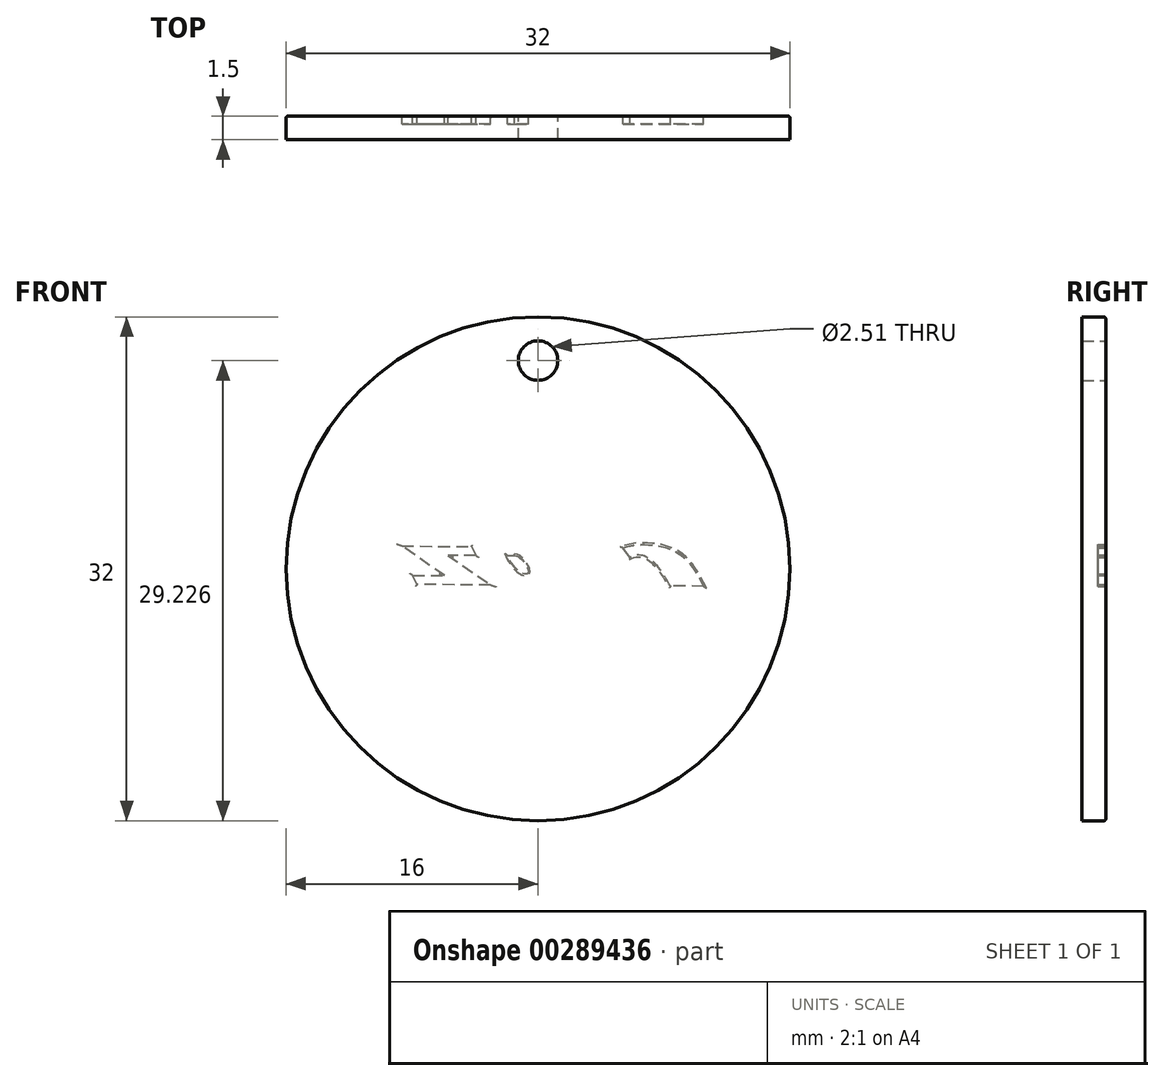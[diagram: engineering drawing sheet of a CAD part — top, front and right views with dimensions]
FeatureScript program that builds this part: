
annotation { "Feature Type Name" : "Feature", "Feature Type Description" : "" }
export const myFeature = defineFeature(function(context is Context, id is Id, definition is map)
    precondition{}
    {
        {
            var Q0;
            Q0=qCreatedBy(makeId("Front.planeOp"),FACE);
            var sketch = newSketch(context, id + "F0", { "sketchPlane" : qUnion([Q0])});
            skCircle(sketch, "E0", {"center": v(0, 0) * mm, "radius": 16 * mm});
            skSolve(sketch);
        }
        {
            var Q0;
            Q0=makeQuery(id+"F0.imprint","IMPRINT",FACE,{"disambiguationData":[TD([[makeQuery(id+"F0.imprint","IMPRINT",EDGE,{"derivedFrom":sQuery(id+"F0.wireOp",EDGE,"E0")}),1.0]])]});
            extrude(context, id + "F1", {"entities" : qUnion([Q0]), "depth" : 1.5 * mm});
        }
        {
            var Q0;
            Q0=qCreatedBy(makeId("Front.planeOp"),FACE);
            var sketch = newSketch(context, id + "F2", { "sketchPlane" : qUnion([Q0])});
            skArc(sketch, "E1.MirrorCS", {"start": v(1.25, -1.6) * mm, "mid": v(1.25, -1.68) * mm, "end": v(1.2, -1.73) * mm});
            skFitSpline(sketch, "E2.MirrorCS", {"points": [v(1.2, -1.73) * mm, v(1.16, -1.75) * mm, v(1.1, -1.78) * mm, v(1.05, -1.8) * mm, v(1.01, -1.82) * mm, v(0.98, -1.83) * mm, v(0.91, -1.86) * mm, v(0.85, -1.88) * mm, v(0.81, -1.9) * mm]});
            skFitSpline(sketch, "E3.MirrorCS", {"points": [v(0.8, -1.22) * mm, v(0.89, -1.2) * mm, v(0.97, -1.17) * mm, v(1.05, -1.15) * mm]});
            skFitSpline(sketch, "E4.MirrorCS", {"points": [v(1.05, -1.15) * mm, v(1.12, -1.3) * mm, v(1.18, -1.45) * mm, v(1.25, -1.6) * mm]});
            skFitSpline(sketch, "E5.MirrorCS", {"points": [v(-1.95, 0.85) * mm, v(-1.8, 0.85) * mm, v(-1.65, 0.85) * mm, v(-1.5, 0.85) * mm]});
            skFitSpline(sketch, "E6.MirrorCS", {"points": [v(-1.5, 0.85) * mm, v(-1.45, 0.84) * mm, v(-1.4, 0.82) * mm, v(-1.34, 0.8) * mm, v(-1.3, 0.8) * mm, v(-1.3, 0.79) * mm, v(-1.27, 0.78) * mm, v(-1.24, 0.76) * mm, v(-1.2, 0.74) * mm, v(-1.16, 0.7) * mm, v(-1.1, 0.67) * mm, v(-1.08, 0.64) * mm, v(-1.03, 0.6) * mm, v(-0.97, 0.53) * mm, v(-0.9, 0.45) * mm, v(-0.85, 0.37) * mm, v(-0.8, 0.3) * mm, v(-0.75, 0.22) * mm, v(-0.72, 0.16) * mm, v(-0.69, 0.1) * mm, v(-0.67, 0.05) * mm, v(-0.65, 0.02) * mm, v(-0.64, 0) * mm, v(-0.64, -0.02) * mm, v(-0.64, -0.03) * mm, v(-0.63, -0.05) * mm, v(-0.63, -0.07) * mm, v(-0.62, -0.1) * mm, v(-0.6, -0.15) * mm, v(-0.61, -0.2) * mm, v(-0.62, -0.22) * mm, v(-0.62, -0.24) * mm, v(-0.63, -0.27) * mm, v(-0.65, -0.3) * mm, v(-0.68, -0.32) * mm, v(-0.72, -0.33) * mm, v(-0.76, -0.34) * mm, v(-0.78, -0.34) * mm, v(-0.8, -0.34) * mm, v(-0.8, -0.34) * mm, v(-0.82, -0.33) * mm, v(-0.85, -0.33) * mm, v(-0.89, -0.32) * mm, v(-0.93, -0.3) * mm, v(-0.97, -0.29) * mm, v(-1, -0.27) * mm, v(-1.02, -0.26) * mm, v(-1.06, -0.24) * mm, v(-1.1, -0.21) * mm, v(-1.19, -0.16) * mm, v(-1.27, -0.1) * mm, v(-1.35, -0.04) * mm, v(-1.41, 0.03) * mm, v(-1.46, 0.08) * mm, v(-1.5, 0.12) * mm, v(-1.53, 0.16) * mm, v(-1.58, 0.22) * mm, v(-1.63, 0.29) * mm, v(-1.68, 0.36) * mm, v(-1.72, 0.41) * mm, v(-1.74, 0.44) * mm, v(-1.75, 0.47) * mm, v(-1.76, 0.49) * mm, v(-1.78, 0.52) * mm, v(-1.8, 0.56) * mm, v(-1.86, 0.67) * mm, v(-1.91, 0.77) * mm, v(-1.95, 0.85) * mm]});
            skFitSpline(sketch, "E7.MirrorCS", {"points": [v(-3.92, 1.36) * mm, v(-3.03, 1.37) * mm, v(-2.15, 1.39) * mm, v(-1.26, 1.4) * mm]});
            skFitSpline(sketch, "E8.MirrorCS", {"points": [v(-5.73, 0.85) * mm, v(-4.83, 0.23) * mm, v(-3.92, -0.4) * mm, v(-3.02, -1.03) * mm]});
            skFitSpline(sketch, "E9.MirrorCS", {"points": [v(-4.22, 1.42) * mm, v(-4.13, 1.23) * mm, v(-4.04, 1.04) * mm, v(-3.95, 0.84) * mm]});
            skFitSpline(sketch, "E10.MirrorCS", {"points": [v(0.82, -0.97) * mm, v(0.78, -1) * mm, v(0.69, -1.03) * mm, v(0.59, -1.05) * mm, v(0.52, -1.06) * mm, v(0.49, -1.06) * mm, v(0.42, -1.07) * mm, v(0.32, -1.07) * mm, v(0.21, -1.07) * mm, v(0.12, -1.07) * mm, v(0, -1.06) * mm, v(-0.14, -1.04) * mm, v(-0.28, -1.01) * mm, v(-0.4, -0.98) * mm, v(-0.54, -0.94) * mm, v(-0.64, -0.9) * mm, v(-0.73, -0.85) * mm, v(-0.78, -0.82) * mm, v(-0.82, -0.8) * mm, v(-0.84, -0.79) * mm, v(-0.85, -0.78) * mm, v(-0.86, -0.78) * mm, v(-0.87, -0.77) * mm, v(-0.9, -0.76) * mm, v(-0.93, -0.73) * mm, v(-1, -0.69) * mm, v(-1.1, -0.62) * mm, v(-1.2, -0.55) * mm, v(-1.25, -0.52) * mm]});
            skFitSpline(sketch, "E11.MirrorCS", {"points": [v(-2.82, -0.75) * mm, v(-3.2, -0.03) * mm, v(-3.57, 0.68) * mm, v(-3.92, 1.36) * mm]});
            skFitSpline(sketch, "E12.MirrorCS", {"points": [v(-1.26, 1.4) * mm, v(-1.06, 1.4) * mm, v(-0.77, 1.36) * mm, v(-0.44, 1.3) * mm, v(-0.28, 1.25) * mm, v(-0.2, 1.22) * mm, v(-0.13, 1.2) * mm, v(-0.05, 1.17) * mm, v(0.04, 1.13) * mm, v(0.15, 1.08) * mm, v(0.26, 1.03) * mm, v(0.34, 0.98) * mm, v(0.4, 0.95) * mm, v(0.46, 0.9) * mm, v(0.52, 0.87) * mm, v(0.57, 0.83) * mm, v(0.6, 0.8) * mm, v(0.64, 0.78) * mm, v(0.65, 0.77) * mm, v(0.68, 0.74) * mm, v(0.74, 0.69) * mm, v(0.8, 0.63) * mm, v(0.84, 0.58) * mm]});
            skFitSpline(sketch, "E13.MirrorCS", {"points": [v(-7.96, -0.42) * mm, v(-7.29, -0.42) * mm, v(-6.61, -0.42) * mm, v(-5.94, -0.43) * mm]});
            skFitSpline(sketch, "E14.MirrorCS", {"points": [v(8.4, -1.1) * mm, v(8.33, -0.97) * mm, v(8.22, -0.78) * mm, v(8.06, -0.53) * mm, v(7.95, -0.35) * mm, v(7.83, -0.15) * mm, v(7.7, 0.02) * mm, v(7.58, 0.16) * mm, v(7.5, 0.26) * mm, v(7.45, 0.3) * mm, v(7.41, 0.34) * mm, v(7.36, 0.4) * mm, v(7.3, 0.45) * mm, v(7.2, 0.54) * mm, v(7.04, 0.65) * mm, v(6.9, 0.74) * mm, v(6.79, 0.79) * mm, v(6.72, 0.81) * mm, v(6.68, 0.83) * mm, v(6.62, 0.84) * mm, v(6.55, 0.86) * mm, v(6.46, 0.87) * mm, v(6.37, 0.88) * mm, v(6.3, 0.88) * mm, v(6.24, 0.87) * mm, v(6.2, 0.86) * mm, v(6.14, 0.85) * mm, v(6.02, 0.82) * mm, v(5.9, 0.77) * mm, v(5.83, 0.73) * mm]});
            skFitSpline(sketch, "E15.MirrorCS", {"points": [v(10.52, -1.1) * mm, v(9.81, -1.1) * mm, v(9.1, -1.1) * mm, v(8.4, -1.1) * mm]});
            skFitSpline(sketch, "E16.MirrorCS", {"points": [v(0.82, 0.62) * mm, v(0.93, 0.48) * mm, v(1.07, 0.28) * mm, v(1.17, 0.04) * mm, v(1.2, -0.08) * mm, v(1.21, -0.15) * mm, v(1.22, -0.2) * mm, v(1.22, -0.27) * mm, v(1.23, -0.35) * mm, v(1.22, -0.44) * mm, v(1.2, -0.55) * mm, v(1.15, -0.68) * mm, v(1.04, -0.83) * mm, v(0.9, -0.93) * mm, v(0.82, -0.97) * mm]});
            skFitSpline(sketch, "E17.MirrorCS", {"points": [v(-8.64, 1.44) * mm, v(-7.17, 1.44) * mm, v(-5.7, 1.43) * mm, v(-4.22, 1.42) * mm]});
            skFitSpline(sketch, "E18.MirrorCS", {"points": [v(-3.02, -1.03) * mm, v(-4.58, -1.02) * mm, v(-6.14, -1) * mm, v(-7.7, -1) * mm]});
            skFitSpline(sketch, "E19.MirrorCS", {"points": [v(5.83, 0.73) * mm, v(5.68, 0.93) * mm, v(5.53, 1.13) * mm, v(5.38, 1.33) * mm]});
            skFitSpline(sketch, "E20.MirrorCS", {"points": [v(-3.95, 0.84) * mm, v(-4.54, 0.85) * mm, v(-5.14, 0.85) * mm, v(-5.73, 0.85) * mm]});
            skFitSpline(sketch, "E21.MirrorCS", {"points": [v(-1.25, -0.52) * mm, v(-1.24, -0.55) * mm, v(-1.21, -0.6) * mm, v(-1.17, -0.67) * mm, v(-1.14, -0.72) * mm, v(-1.13, -0.75) * mm, v(-1.11, -0.77) * mm, v(-1.1, -0.78) * mm, v(-1.1, -0.8) * mm, v(-1.08, -0.82) * mm, v(-1.05, -0.86) * mm, v(-1.01, -0.91) * mm, v(-0.96, -0.97) * mm, v(-0.9, -1.03) * mm, v(-0.8, -1.1) * mm, v(-0.68, -1.18) * mm, v(-0.56, -1.23) * mm, v(-0.47, -1.26) * mm, v(-0.42, -1.28) * mm, v(-0.38, -1.29) * mm, v(-0.34, -1.3) * mm, v(-0.3, -1.3) * mm, v(-0.21, -1.32) * mm, v(-0.12, -1.33) * mm, v(-0.01, -1.33) * mm, v(0.06, -1.33) * mm, v(0.13, -1.33) * mm, v(0.18, -1.32) * mm, v(0.2, -1.32) * mm, v(0.23, -1.32) * mm, v(0.24, -1.32) * mm, v(0.26, -1.32) * mm, v(0.3, -1.31) * mm, v(0.34, -1.3) * mm, v(0.41, -1.3) * mm, v(0.5, -1.28) * mm, v(0.64, -1.25) * mm, v(0.76, -1.23) * mm, v(0.82, -1.21) * mm]});
            skFitSpline(sketch, "E22.MirrorCS", {"points": [v(-7.7, -1) * mm, v(-7.79, -0.8) * mm, v(-7.87, -0.61) * mm, v(-7.96, -0.42) * mm]});
            skFitSpline(sketch, "E23.MirrorCS", {"points": [v(-5.94, -0.43) * mm, v(-6.84, 0.2) * mm, v(-7.74, 0.82) * mm, v(-8.64, 1.44) * mm]});
            skFitSpline(sketch, "E24.MirrorCS", {"points": [v(0.83, -1.89) * mm, v(0.7, -1.92) * mm, v(0.46, -1.95) * mm, v(0.1, -1.98) * mm, v(-0.14, -1.98) * mm, v(-0.35, -1.98) * mm, v(-0.54, -1.98) * mm, v(-0.72, -1.97) * mm, v(-0.88, -1.96) * mm, v(-1, -1.94) * mm, v(-1.1, -1.93) * mm, v(-1.16, -1.92) * mm, v(-1.2, -1.92) * mm, v(-1.21, -1.91) * mm, v(-1.25, -1.9) * mm, v(-1.3, -1.9) * mm, v(-1.37, -1.88) * mm, v(-1.47, -1.85) * mm, v(-1.6, -1.81) * mm, v(-1.76, -1.75) * mm, v(-1.9, -1.68) * mm, v(-2.05, -1.6) * mm, v(-2.16, -1.53) * mm, v(-2.27, -1.45) * mm, v(-2.36, -1.36) * mm, v(-2.46, -1.27) * mm, v(-2.53, -1.2) * mm, v(-2.58, -1.13) * mm, v(-2.62, -1.08) * mm, v(-2.66, -1.04) * mm, v(-2.68, -1) * mm, v(-2.7, -0.98) * mm, v(-2.7, -0.96) * mm, v(-2.73, -0.93) * mm, v(-2.76, -0.87) * mm, v(-2.8, -0.8) * mm, v(-2.82, -0.75) * mm]});
            skFitSpline(sketch, "E25.MirrorCS", {"points": [v(5.38, 1.33) * mm, v(5.48, 1.37) * mm, v(5.7, 1.44) * mm, v(6.02, 1.5) * mm, v(6.28, 1.52) * mm, v(6.5, 1.53) * mm, v(6.67, 1.54) * mm, v(6.82, 1.54) * mm, v(6.94, 1.53) * mm, v(7.04, 1.53) * mm, v(7.19, 1.52) * mm, v(7.43, 1.5) * mm, v(7.76, 1.45) * mm, v(8.07, 1.37) * mm, v(8.28, 1.3) * mm, v(8.38, 1.26) * mm, v(8.44, 1.23) * mm, v(8.48, 1.22) * mm, v(8.53, 1.2) * mm, v(8.6, 1.17) * mm, v(8.7, 1.12) * mm, v(8.85, 1.04) * mm, v(8.98, 0.95) * mm, v(9.08, 0.87) * mm, v(9.16, 0.81) * mm, v(9.22, 0.76) * mm, v(9.31, 0.68) * mm, v(9.43, 0.57) * mm, v(9.54, 0.44) * mm, v(9.62, 0.34) * mm, v(9.67, 0.29) * mm, v(9.7, 0.24) * mm, v(9.73, 0.2) * mm, v(9.77, 0.15) * mm, v(9.84, 0.06) * mm, v(9.92, -0.05) * mm, v(9.99, -0.16) * mm, v(10.04, -0.24) * mm, v(10.09, -0.3) * mm, v(10.12, -0.36) * mm, v(10.14, -0.39) * mm, v(10.15, -0.41) * mm, v(10.16, -0.42) * mm, v(10.17, -0.45) * mm, v(10.2, -0.48) * mm, v(10.23, -0.54) * mm, v(10.27, -0.62) * mm, v(10.33, -0.73) * mm, v(10.4, -0.89) * mm, v(10.48, -1.03) * mm, v(10.52, -1.1) * mm]});
            skFitSpline(sketch, "E26.MirrorC", {"points": [v(3.04, 1.45) * mm, v(3.14, 1.45) * mm, v(3.22, 1.44) * mm, v(3.34, 1.44) * mm, v(3.49, 1.43) * mm, v(3.64, 1.42) * mm, v(3.77, 1.4) * mm, v(3.86, 1.4) * mm, v(3.96, 1.38) * mm, v(4.1, 1.36) * mm, v(4.25, 1.33) * mm, v(4.39, 1.3) * mm, v(4.48, 1.27) * mm, v(4.54, 1.25) * mm, v(4.57, 1.24) * mm, v(4.62, 1.23) * mm, v(4.68, 1.2) * mm, v(4.78, 1.17) * mm, v(4.92, 1.1) * mm, v(5.08, 1.03) * mm, v(5.23, 0.94) * mm, v(5.38, 0.82) * mm, v(5.49, 0.73) * mm, v(5.57, 0.63) * mm, v(5.63, 0.56) * mm, v(5.7, 0.5) * mm, v(5.74, 0.42) * mm, v(5.79, 0.34) * mm, v(5.83, 0.26) * mm, v(5.87, 0.18) * mm, v(5.9, 0.06) * mm, v(5.93, -0.1) * mm, v(5.93, -0.24) * mm, v(5.9, -0.36) * mm, v(5.88, -0.44) * mm, v(5.84, -0.53) * mm, v(5.79, -0.6) * mm, v(5.74, -0.67) * mm, v(5.67, -0.74) * mm, v(5.61, -0.78) * mm, v(5.56, -0.82) * mm, v(5.52, -0.85) * mm, v(5.49, -0.87) * mm, v(5.44, -0.9) * mm, v(5.37, -0.93) * mm, v(5.3, -0.96) * mm, v(5.24, -0.98) * mm, v(5.19, -1) * mm, v(5.15, -1) * mm, v(5.1, -1.02) * mm, v(5.03, -1.04) * mm, v(4.95, -1.05) * mm, v(4.89, -1.07) * mm, v(4.83, -1.08) * mm, v(4.8, -1.08) * mm, v(4.73, -1.1) * mm, v(4.63, -1.1) * mm, v(4.48, -1.12) * mm, v(4.3, -1.14) * mm, v(4.05, -1.14) * mm, v(3.8, -1.14) * mm, v(3.6, -1.13) * mm, v(3.48, -1.11) * mm, v(3.39, -1.1) * mm, v(3.3, -1.1) * mm, v(3.17, -1.07) * mm, v(3.02, -1.04) * mm, v(2.87, -1) * mm, v(2.77, -0.98) * mm, v(2.72, -0.97) * mm, v(2.68, -0.95) * mm, v(2.63, -0.94) * mm, v(2.57, -0.92) * mm, v(2.46, -0.88) * mm, v(2.32, -0.82) * mm, v(2.19, -0.75) * mm, v(2.09, -0.7) * mm, v(2.02, -0.65) * mm, v(1.94, -0.6) * mm, v(1.85, -0.52) * mm, v(1.74, -0.42) * mm, v(1.64, -0.3) * mm, v(1.57, -0.22) * mm, v(1.54, -0.17) * mm, v(1.51, -0.13) * mm, v(1.48, -0.09) * mm, v(1.45, -0.03) * mm, v(1.4, 0.05) * mm, v(1.37, 0.14) * mm, v(1.33, 0.25) * mm, v(1.31, 0.37) * mm, v(1.31, 0.47) * mm, v(1.32, 0.55) * mm, v(1.34, 0.64) * mm, v(1.38, 0.74) * mm, v(1.43, 0.84) * mm, v(1.5, 0.94) * mm, v(1.58, 1) * mm, v(1.64, 1.06) * mm, v(1.69, 1.1) * mm, v(1.72, 1.1) * mm, v(1.74, 1.13) * mm, v(1.76, 1.14) * mm, v(1.78, 1.15) * mm, v(1.82, 1.17) * mm, v(1.9, 1.22) * mm, v(2.04, 1.28) * mm, v(2.19, 1.33) * mm, v(2.3, 1.36) * mm, v(2.36, 1.37) * mm, v(2.42, 1.38) * mm, v(2.46, 1.39) * mm, v(2.51, 1.4) * mm, v(2.61, 1.42) * mm, v(2.76, 1.43) * mm, v(2.92, 1.44) * mm, v(3.04, 1.45) * mm, v(3.14, 1.45) * mm, v(3.22, 1.44) * mm, v(3.04, 1.45) * mm]});
            skFitSpline(sketch, "E27.MirrorC", {"points": [v(3.29, 0.8) * mm, v(3.33, 0.8) * mm, v(3.36, 0.8) * mm, v(3.4, 0.8) * mm, v(3.47, 0.79) * mm, v(3.56, 0.76) * mm, v(3.64, 0.71) * mm, v(3.7, 0.67) * mm, v(3.73, 0.64) * mm, v(3.76, 0.62) * mm, v(3.78, 0.6) * mm, v(3.8, 0.58) * mm, v(3.84, 0.54) * mm, v(3.87, 0.5) * mm, v(3.91, 0.44) * mm, v(3.95, 0.39) * mm, v(4, 0.32) * mm, v(4.04, 0.24) * mm, v(4.08, 0.14) * mm, v(4.11, 0.07) * mm, v(4.13, 0.02) * mm, v(4.15, -0.05) * mm, v(4.16, -0.1) * mm, v(4.17, -0.16) * mm, v(4.18, -0.2) * mm, v(4.18, -0.22) * mm, v(4.18, -0.25) * mm, v(4.18, -0.28) * mm, v(4.18, -0.3) * mm, v(4.17, -0.36) * mm, v(4.16, -0.4) * mm, v(4.14, -0.43) * mm, v(4.12, -0.45) * mm, v(4.1, -0.46) * mm, v(4.08, -0.48) * mm, v(4.03, -0.49) * mm, v(3.98, -0.5) * mm, v(3.93, -0.5) * mm, v(3.89, -0.5) * mm, v(3.86, -0.5) * mm, v(3.82, -0.5) * mm, v(3.75, -0.49) * mm, v(3.65, -0.46) * mm, v(3.57, -0.41) * mm, v(3.51, -0.37) * mm, v(3.48, -0.35) * mm, v(3.46, -0.32) * mm, v(3.44, -0.3) * mm, v(3.42, -0.28) * mm, v(3.38, -0.24) * mm, v(3.35, -0.2) * mm, v(3.3, -0.12) * mm, v(3.24, -0.05) * mm, v(3.2, 0) * mm, v(3.2, 0.04) * mm, v(3.18, 0.06) * mm, v(3.16, 0.1) * mm, v(3.14, 0.13) * mm, v(3.12, 0.17) * mm, v(3.1, 0.22) * mm, v(3.07, 0.3) * mm, v(3.05, 0.38) * mm, v(3.04, 0.45) * mm, v(3.03, 0.49) * mm, v(3.03, 0.51) * mm, v(3.03, 0.55) * mm, v(3.03, 0.6) * mm, v(3.04, 0.64) * mm, v(3.06, 0.7) * mm, v(3.1, 0.75) * mm, v(3.17, 0.78) * mm, v(3.24, 0.8) * mm, v(3.29, 0.8) * mm, v(3.33, 0.8) * mm, v(3.36, 0.8) * mm, v(3.29, 0.8) * mm]});
            skSolve(sketch);
        }
        {
            var Q0;
            Q0 = qSketchRegion(id + "F2", true);
            extrude(context, id + "F3", {"entities" : qUnion([Q0]), "operationType" : NewBodyOperationType.REMOVE, "depth" : 0.5 * mm});
        }
        {
            var Q0;
            Q0=makeQuery(id+"F3.boolean.opBoolean","COPY",EDGE,{"derivedFrom":makeQuery(id+"F3.opExtrude","CAP_EDGE",EDGE,{"disambiguationData":[OSD([sQuery(id+"F2.wireOp",EDGE,"E25.MirrorCS")])],"isStart":true})});
            var Q1;
            Q1=makeQuery(id+"F3.boolean.opBoolean","COPY",EDGE,{"derivedFrom":makeQuery(id+"F3.opExtrude","CAP_EDGE",EDGE,{"disambiguationData":[OSD([sQuery(id+"F2.wireOp",EDGE,"E15.MirrorCS")])],"isStart":true})});
            var Q2;
            Q2=makeQuery(id+"F3.boolean.opBoolean","COPY",EDGE,{"derivedFrom":makeQuery(id+"F3.opExtrude","CAP_EDGE",EDGE,{"disambiguationData":[OSD([sQuery(id+"F2.wireOp",EDGE,"E14.MirrorCS")])],"isStart":true})});
            var Q3;
            Q3=makeQuery(id+"F3.boolean.opBoolean","COPY",EDGE,{"derivedFrom":makeQuery(id+"F3.opExtrude","CAP_EDGE",EDGE,{"disambiguationData":[OSD([sQuery(id+"F2.wireOp",EDGE,"E19.MirrorCS")])],"isStart":true})});
            var Q4;
            Q4=makeQuery(id+"F3.boolean.opBoolean","COPY",EDGE,{"derivedFrom":makeQuery(id+"F3.opExtrude","CAP_EDGE",EDGE,{"disambiguationData":[OSD([sQuery(id+"F2.wireOp",EDGE,"E27.MirrorC")])],"isStart":true})});
            var Q5;
            Q5=makeQuery(id+"F3.boolean.opBoolean","COPY",EDGE,{"derivedFrom":makeQuery(id+"F3.opExtrude","CAP_EDGE",EDGE,{"disambiguationData":[OSD([sQuery(id+"F2.wireOp",EDGE,"E26.MirrorC")])],"isStart":true})});
            var Q6;
            Q6=makeQuery(id+"F3.boolean.opBoolean","COPY",EDGE,{"derivedFrom":makeQuery(id+"F3.opExtrude","CAP_EDGE",EDGE,{"disambiguationData":[OSD([sQuery(id+"F2.wireOp",EDGE,"E12.MirrorCS")])],"isStart":true})});
            var Q7;
            Q7=makeQuery(id+"F3.boolean.opBoolean","COPY",EDGE,{"derivedFrom":makeQuery(id+"F3.opExtrude","CAP_EDGE",EDGE,{"disambiguationData":[OSD([sQuery(id+"F2.wireOp",EDGE,"E16.MirrorCS")])],"isStart":true})});
            var Q8;
            Q8=makeQuery(id+"F3.boolean.opBoolean","COPY",EDGE,{"derivedFrom":makeQuery(id+"F3.opExtrude","CAP_EDGE",EDGE,{"disambiguationData":[OSD([sQuery(id+"F2.wireOp",EDGE,"E10.MirrorCS")])],"isStart":true})});
            var Q9;
            Q9=makeQuery(id+"F3.boolean.opBoolean","COPY",EDGE,{"derivedFrom":makeQuery(id+"F3.opExtrude","CAP_EDGE",EDGE,{"disambiguationData":[OSD([sQuery(id+"F2.wireOp",EDGE,"E21.MirrorCS")])],"isStart":true})});
            var Q10;
            Q10=makeQuery(id+"F3.boolean.opBoolean","COPY",EDGE,{"derivedFrom":makeQuery(id+"F3.opExtrude","CAP_EDGE",EDGE,{"disambiguationData":[OSD([sQuery(id+"F2.wireOp",EDGE,"E3.MirrorCS")])],"isStart":true})});
            var Q11;
            Q11=makeQuery(id+"F3.boolean.opBoolean","COPY",EDGE,{"derivedFrom":makeQuery(id+"F3.opExtrude","CAP_EDGE",EDGE,{"disambiguationData":[OSD([sQuery(id+"F2.wireOp",EDGE,"E4.MirrorCS")])],"isStart":true})});
            var Q12;
            Q12=makeQuery(id+"F3.boolean.opBoolean","COPY",EDGE,{"derivedFrom":makeQuery(id+"F3.opExtrude","CAP_EDGE",EDGE,{"disambiguationData":[OSD([sQuery(id+"F2.wireOp",EDGE,"E1.MirrorCS")])],"isStart":true})});
            var Q13;
            Q13=makeQuery(id+"F3.boolean.opBoolean","COPY",EDGE,{"derivedFrom":makeQuery(id+"F3.opExtrude","CAP_EDGE",EDGE,{"disambiguationData":[OSD([sQuery(id+"F2.wireOp",EDGE,"E24.MirrorCS")])],"isStart":true})});
            var Q14;
            Q14=makeQuery(id+"F3.boolean.opBoolean","COPY",EDGE,{"derivedFrom":makeQuery(id+"F3.opExtrude","CAP_EDGE",EDGE,{"disambiguationData":[OSD([sQuery(id+"F2.wireOp",EDGE,"E11.MirrorCS")])],"isStart":true})});
            var Q15;
            Q15=makeQuery(id+"F3.boolean.opBoolean","COPY",EDGE,{"derivedFrom":makeQuery(id+"F3.opExtrude","CAP_EDGE",EDGE,{"disambiguationData":[OSD([sQuery(id+"F2.wireOp",EDGE,"E7.MirrorCS")])],"isStart":true})});
            var Q16;
            Q16=makeQuery(id+"F3.boolean.opBoolean","SPLIT",FACE,{"disambiguationData":[TD([makeQuery(id+"F3.opExtrude","SWEPT_FACE",FACE,{"disambiguationData":[OSD([sQuery(id+"F2.wireOp",EDGE,"E5.MirrorCS")])]})])],"derivedFrom":makeQuery(id+"F1.opExtrude","CAP_FACE",FACE,{"disambiguationData":[OSD([sQuery(id+"F0.wireOp",EDGE,"E0")])],"isStart":true})});
            var Q17;
            Q17=makeQuery(id+"F3.boolean.opBoolean","COPY",EDGE,{"derivedFrom":makeQuery(id+"F3.opExtrude","CAP_EDGE",EDGE,{"disambiguationData":[OSD([sQuery(id+"F2.wireOp",EDGE,"E20.MirrorCS")])],"isStart":true})});
            var Q18;
            Q18=makeQuery(id+"F3.boolean.opBoolean","COPY",EDGE,{"derivedFrom":makeQuery(id+"F3.opExtrude","CAP_EDGE",EDGE,{"disambiguationData":[OSD([sQuery(id+"F2.wireOp",EDGE,"E9.MirrorCS")])],"isStart":true})});
            var Q19;
            Q19=makeQuery(id+"F3.boolean.opBoolean","COPY",EDGE,{"derivedFrom":makeQuery(id+"F3.opExtrude","CAP_EDGE",EDGE,{"disambiguationData":[OSD([sQuery(id+"F2.wireOp",EDGE,"E17.MirrorCS")])],"isStart":true})});
            var Q20;
            Q20=makeQuery(id+"F3.boolean.opBoolean","COPY",EDGE,{"derivedFrom":makeQuery(id+"F3.opExtrude","CAP_EDGE",EDGE,{"disambiguationData":[OSD([sQuery(id+"F2.wireOp",EDGE,"E23.MirrorCS")])],"isStart":true})});
            var Q21;
            Q21=makeQuery(id+"F3.boolean.opBoolean","COPY",EDGE,{"derivedFrom":makeQuery(id+"F3.opExtrude","CAP_EDGE",EDGE,{"disambiguationData":[OSD([sQuery(id+"F2.wireOp",EDGE,"E13.MirrorCS")])],"isStart":true})});
            var Q22;
            Q22=makeQuery(id+"F3.boolean.opBoolean","COPY",EDGE,{"derivedFrom":makeQuery(id+"F3.opExtrude","CAP_EDGE",EDGE,{"disambiguationData":[OSD([sQuery(id+"F2.wireOp",EDGE,"E22.MirrorCS")])],"isStart":true})});
            var Q23;
            Q23=makeQuery(id+"F3.boolean.opBoolean","COPY",EDGE,{"derivedFrom":makeQuery(id+"F3.opExtrude","CAP_EDGE",EDGE,{"disambiguationData":[OSD([sQuery(id+"F2.wireOp",EDGE,"E18.MirrorCS")])],"isStart":true})});
            var Q24;
            Q24=makeQuery(id+"F3.boolean.opBoolean","COPY",EDGE,{"derivedFrom":makeQuery(id+"F3.opExtrude","CAP_EDGE",EDGE,{"disambiguationData":[OSD([sQuery(id+"F2.wireOp",EDGE,"E8.MirrorCS")])],"isStart":true})});
            var Q25;
            Q25=makeQuery(id+"F3.boolean.opBoolean","COPY",EDGE,{"derivedFrom":makeQuery(id+"F3.opExtrude","CAP_EDGE",EDGE,{"disambiguationData":[OSD([sQuery(id+"F2.wireOp",EDGE,"E2.MirrorCS")])],"isStart":true})});
            fillet(context, id + "F4", {"entities" : qUnion([Q0, Q1, Q2, Q3, Q4, Q5, Q6, Q7, Q8, Q9, Q10, Q11, Q12, Q13, Q14, Q15, Q16, Q17, Q18, Q19, Q20, Q21, Q22, Q23, Q24, Q25]), "radius" : 0.1 * mm, "tangentPropagation" : true, "allowEdgeOverflow" : false});
        }
        {
            var Q0;
            Q0=qCreatedBy(makeId("Front.planeOp"),FACE);
            var sketch = newSketch(context, id + "F5", { "sketchPlane" : qUnion([Q0])});
            skCircle(sketch, "E28", {"center": v(0, 13.23) * mm, "radius": 1.25 * mm});
            skSolve(sketch);
        }
        {
            var Q0;
            Q0=makeQuery(id+"F5.imprint","IMPRINT",FACE,{"disambiguationData":[TD([[makeQuery(id+"F5.imprint","IMPRINT",EDGE,{"derivedFrom":sQuery(id+"F5.wireOp",EDGE,"E28")}),1.0]])]});
            extrude(context, id + "F6", {"entities" : qUnion([Q0]), "operationType" : NewBodyOperationType.REMOVE, "depth" : 25 * mm});
        }
    });
